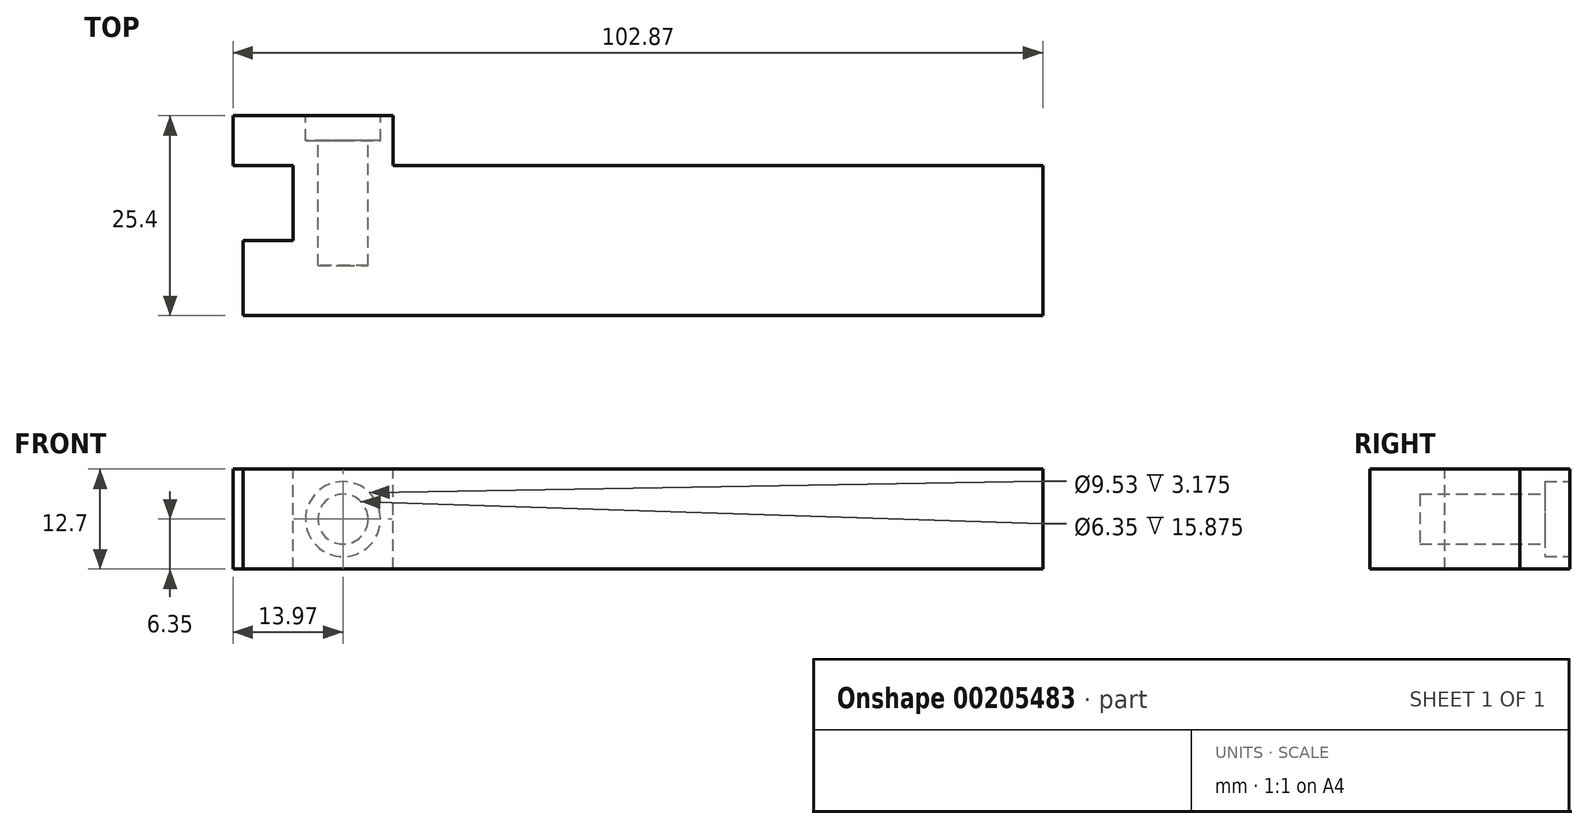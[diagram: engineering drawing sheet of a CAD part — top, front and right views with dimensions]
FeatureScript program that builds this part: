
annotation { "Feature Type Name" : "Feature", "Feature Type Description" : "" }
export const myFeature = defineFeature(function(context is Context, id is Id, definition is map)
    precondition{}
    {
        {
            var Q0;
            Q0=qCreatedBy(makeId("Front.planeOp"),FACE);
            var sketch = newSketch(context, id + "F0", { "sketchPlane" : qUnion([Q0])});
            skLineSegment(sketch, "E0.bottom", {"start": v(0, 0) * mm, "end": v(101.6, 0) * mm});
            skLineSegment(sketch, "E0.top", {"start": v(0, 12.7) * mm, "end": v(101.6, 12.7) * mm});
            skLineSegment(sketch, "E0.left", {"start": v(0, 0) * mm, "end": v(0, 12.7) * mm});
            skLineSegment(sketch, "E0.right", {"start": v(101.6, 0) * mm, "end": v(101.6, 12.7) * mm});
            skSolve(sketch);
        }
        {
            var Q0;
            Q0=makeQuery(id+"F0.imprint","IMPRINT",FACE,{"disambiguationData":[TD([[makeQuery(id+"F0.imprint","IMPRINT",EDGE,{"derivedFrom":sQuery(id+"F0.wireOp",EDGE,"E0.bottom")}),1.0]])]});
            extrude(context, id + "F1", {"entities" : qUnion([Q0]), "depth" : 19.05 * mm});
        }
        {
            var Q0;
            Q0=makeQuery(id+"F1.opExtrude","SWEPT_FACE",FACE,{"disambiguationData":[OSD([sQuery(id+"F0.wireOp",EDGE,"E0.top")])]});
            var sketch = newSketch(context, id + "F2", { "sketchPlane" : qUnion([Q0])});
            skLineSegment(sketch, "E1.bottom", {"start": v(0, 0) * mm, "end": v(6.35, 0) * mm});
            skLineSegment(sketch, "E1.top", {"start": v(0, -9.52) * mm, "end": v(6.35, -9.52) * mm});
            skLineSegment(sketch, "E1.left", {"start": v(0, 0) * mm, "end": v(0, -9.52) * mm});
            skLineSegment(sketch, "E1.right", {"start": v(6.35, 0) * mm, "end": v(6.35, -9.52) * mm});
            skSolve(sketch);
        }
        {
            var Q0;
            Q0=makeQuery(id+"F2.imprint","IMPRINT",FACE,{"disambiguationData":[TD([[makeQuery(id+"F2.imprint","IMPRINT",EDGE,{"derivedFrom":sQuery(id+"F2.wireOp",EDGE,"E1.bottom")}),-1.0]])]});
            extrude(context, id + "F3", {"entities" : qUnion([Q0]), "operationType" : NewBodyOperationType.REMOVE, "oppositeDirection" : true, "depth" : 25.4 * mm});
        }
        {
            var Q0;
            Q0=makeQuery(id+"F1.opExtrude","CAP_FACE",FACE,{"disambiguationData":[OSD([sQuery(id+"F0.wireOp",EDGE,"E0.bottom"),sQuery(id+"F0.wireOp",EDGE,"E0.top"),sQuery(id+"F0.wireOp",EDGE,"E0.left"),sQuery(id+"F0.wireOp",EDGE,"E0.right")])],"isStart":true});
            var sketch = newSketch(context, id + "F4", { "sketchPlane" : qUnion([Q0])});
            skCircle(sketch, "E2", {"center": v(-12.7, 6.35) * mm, "radius": 3.18 * mm});
            skPoint(sketch, "E3", {"position": v(-6.35, 6.35) * mm});
            skSolve(sketch);
        }
        {
            var Q0;
            Q0=makeQuery(id+"F1.opExtrude","CAP_FACE",FACE,{"disambiguationData":[OSD([sQuery(id+"F0.wireOp",EDGE,"E0.bottom"),sQuery(id+"F0.wireOp",EDGE,"E0.top"),sQuery(id+"F0.wireOp",EDGE,"E0.left"),sQuery(id+"F0.wireOp",EDGE,"E0.right")])],"isStart":true});
            var sketch = newSketch(context, id + "F5", { "sketchPlane" : qUnion([Q0])});
            skSolve(sketch);
        }
        {
            var Q0;
            Q0=makeQuery(id+"F4.imprint","IMPRINT",FACE,{"disambiguationData":[TD([[makeQuery(id+"F4.imprint","IMPRINT",EDGE,{"derivedFrom":sQuery(id+"F4.wireOp",EDGE,"E2")}),1.0]])]});
            extrude(context, id + "F6", {"entities" : qUnion([Q0]), "operationType" : NewBodyOperationType.REMOVE, "oppositeDirection" : true, "depth" : 12.7 * mm});
        }
        {
            var Q0;
            Q0=makeQuery(id+"F5.imprint","IMPRINT",FACE,{"disambiguationData":[TD([[makeQuery(id+"F5.imprint","IMPRINT",EDGE,{"derivedFrom":makeQuery(id+"F1.opExtrude","CAP_EDGE",EDGE,{"disambiguationData":[OSD([sQuery(id+"F0.wireOp",EDGE,"E0.right")])],"isStart":true})}),-1.0]])]});
            var sketch = newSketch(context, id + "F7", { "sketchPlane" : qUnion([Q0])});
            skLineSegment(sketch, "E4.bottom", {"start": v(-19.05, 0) * mm, "end": v(1.27, 0) * mm});
            skLineSegment(sketch, "E4.top", {"start": v(-19.05, 12.7) * mm, "end": v(1.27, 12.7) * mm});
            skLineSegment(sketch, "E4.left", {"start": v(-19.05, 0) * mm, "end": v(-19.05, 12.7) * mm});
            skLineSegment(sketch, "E4.right", {"start": v(1.27, 0) * mm, "end": v(1.27, 12.7) * mm});
            skSolve(sketch);
        }
        {
            var Q0;
            Q0 = qSketchRegion(id + "F7", true);
            extrude(context, id + "F8", {"entities" : qUnion([Q0]), "operationType" : NewBodyOperationType.ADD, "depth" : 6.35 * mm});
        }
        {
            var Q0;
            Q0=makeQuery(id+"F8.opExtrude","CAP_FACE",FACE,{"disambiguationData":[OSD([sQuery(id+"F7.wireOp",EDGE,"E4.bottom"),sQuery(id+"F7.wireOp",EDGE,"E4.top"),sQuery(id+"F7.wireOp",EDGE,"E4.left"),sQuery(id+"F7.wireOp",EDGE,"E4.right")])],"isStart":false});
            var sketch = newSketch(context, id + "F9", { "sketchPlane" : qUnion([Q0])});
            skCircle(sketch, "E5", {"center": v(-12.7, 6.35) * mm, "radius": 4.76 * mm});
            skLineSegment(sketch, "E6", {"start": v(-12.7, 6.35) * mm, "end": v(-19.05, 6.35) * mm, "construction": true});
            skPoint(sketch, "E6.endSnap0", {"position": v(-19.05, 6.35) * mm});
            skCircle(sketch, "E7", {"center": v(-12.7, 6.35) * mm, "radius": 3.18 * mm});
            skSolve(sketch);
        }
        {
            var Q0;
            Q0 = qSketchRegion(id + "F9", true);
            extrude(context, id + "F10", {"entities" : qUnion([Q0]), "operationType" : NewBodyOperationType.REMOVE, "oppositeDirection" : true, "depth" : 3.17 * mm});
        }
        {
            var Q0;
            Q0=makeQuery(id+"F10.boolean.opBoolean","SPLIT",FACE,{"disambiguationData":[TD([makeQuery(id+"F10.opExtrude","SWEPT_FACE",FACE,{"disambiguationData":[OSD([sQuery(id+"F9.wireOp",EDGE,"E7")])]})])],"derivedFrom":makeQuery(id+"F8.opExtrude","CAP_FACE",FACE,{"disambiguationData":[OSD([sQuery(id+"F7.wireOp",EDGE,"E4.bottom"),sQuery(id+"F7.wireOp",EDGE,"E4.top"),sQuery(id+"F7.wireOp",EDGE,"E4.left"),sQuery(id+"F7.wireOp",EDGE,"E4.right")])],"isStart":false})});
            extrude(context, id + "F11", {"entities" : qUnion([Q0]), "operationType" : NewBodyOperationType.REMOVE, "oppositeDirection" : true, "depth" : 6.35 * mm});
        }
    });
